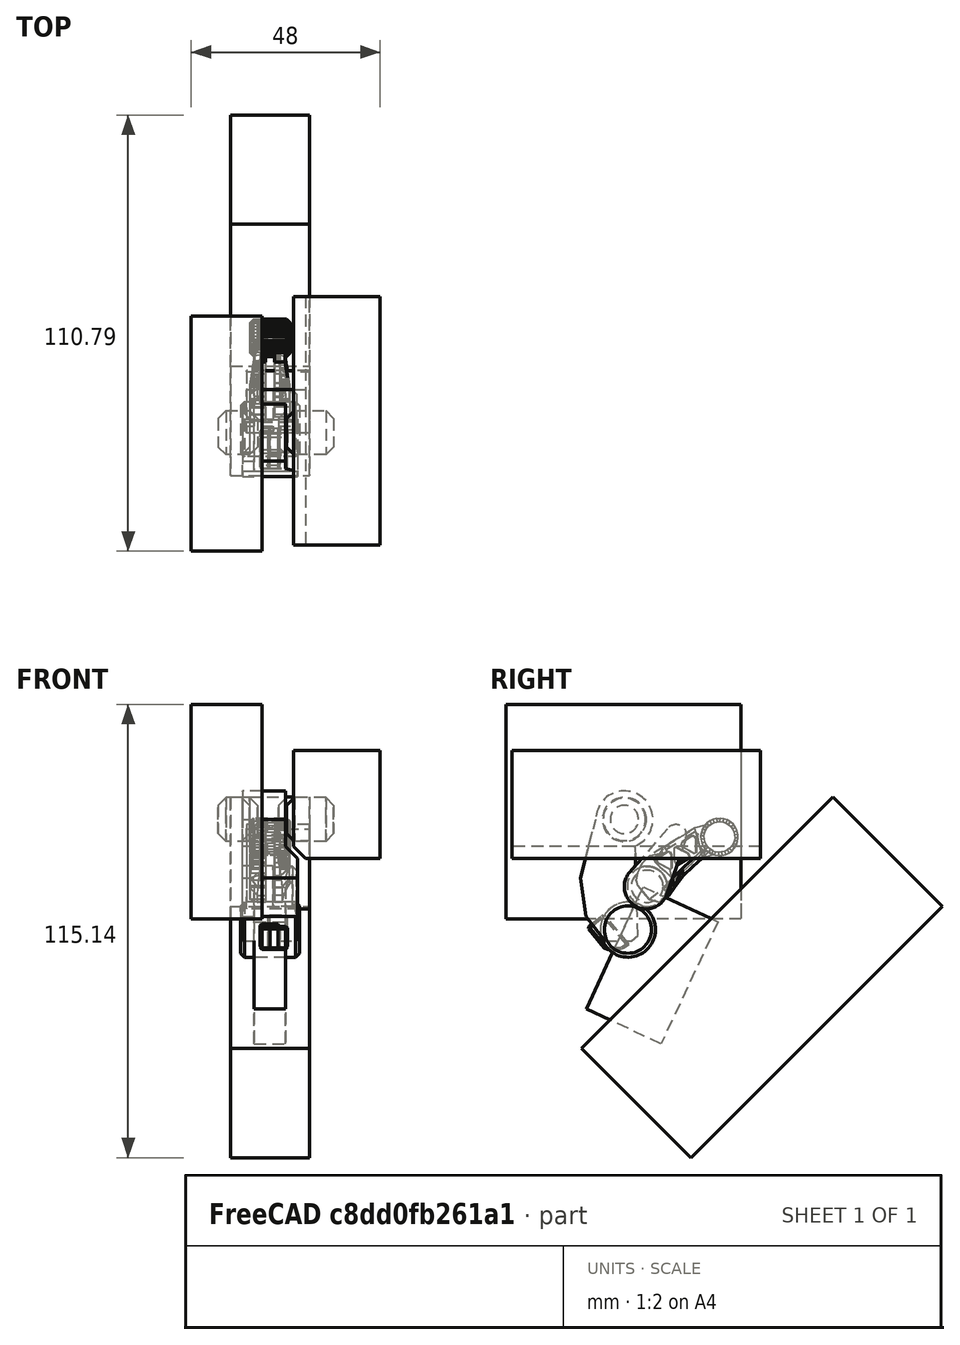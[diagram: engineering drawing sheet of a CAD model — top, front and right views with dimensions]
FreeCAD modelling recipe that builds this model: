
FCSTD DOCUMENT  (FreeCAD 0.21R33771 (Git))
Label: MechaLeg01
License: All rights reserved
LicenseURL: http://en.wikipedia.org/wiki/All_rights_reserved
objects: PartDesign::Body×12, Sketcher::SketchObject×11, PartDesign::Pad×11, PartDesign::Boolean×7, PartDesign::Chamfer×6, Part::Feature×2, Mesh::Feature×1, Part::Refine×1, PartDesign::FeatureBase×1
note: 68 computed .brp shape members not serialized (recipe doc carries the construction recipe); baked Part::Feature solids carry a one-line shape summary decoded from their .brp

FEATURE [Sketcher::SketchObject] Sketch
  FullyConstrained = false
  MapMode = 5
  Placement = pos=(0,0,0) rot=(0.57735,0.57735,0.57735;2.0944rad)
  Support = -> [YZ_Plane]
  sketch-geometry (7):
    g0: LineSegment StartX=-4.95735 StartY=-30.9168 StartZ=0 EndX=-9.7066 EndY=-24.689 EndZ=0
    g1: ArcOfCircle CenterX=0 CenterY=0 CenterZ=0 NormalX=0 NormalY=0 NormalZ=1 AngleXU=0 Radius=7.23735 StartAngle=5.09534 EndAngle=9.42478
    g2: LineSegment StartX=-4.95735 StartY=-30.9168 StartZ=0 EndX=1.76245 EndY=-30.9168 EndZ=0
    g3: LineSegment StartX=1.76245 StartY=-30.9168 StartZ=0 EndX=3.46482 EndY=-29.4243 EndZ=0
    g4: LineSegment StartX=3.46482 StartY=-29.4243 StartZ=0 EndX=2.70427 EndY=-6.71313 EndZ=0
    g5: LineSegment StartX=-9.7066 StartY=-24.689 StartZ=0 EndX=-11.1541 EndY=-14.812 EndZ=0
    g6: LineSegment StartX=-11.1541 StartY=-14.812 StartZ=0 EndX=-7.23735 EndY=1.8e-15 EndZ=0
  constraints (10):
    c: PointOnObject(g1,g-1)
    c: Coincident(g1,g-1)
    c: Coincident(g2,g0)
    c: Horizontal(g2)
    c: Coincident(g3,g2)
    c: Coincident(g4,g3)
    c: Coincident(g1,g4)
    c: Coincident(g5,g0)
    c: Coincident(g6,g5)
    c: Coincident(g6,g1)
FEATURE [PartDesign::Pad] Pad
  Direction = (1,-2e-16,3e-16)
  Length = 14
  Length2 = 10
  Placement = pos=(0,0,0) rot=(1,1,1;2.0944rad)
  Profile = -> Sketch
  ReferenceAxis = -> Sketch [N_Axis]
  Type = 0
FEATURE [Sketcher::SketchObject] Sketch001
  FullyConstrained = false
  MapMode = 5
  Placement = pos=(0,0,0) rot=(0.57735,0.57735,0.57735;2.0944rad)
  Support = -> [YZ_Plane001]
  sketch-geometry (1):
    g0: Circle CenterX=0 CenterY=0 CenterZ=0 NormalX=0 NormalY=0 NormalZ=1 AngleXU=0 Radius=5.59018
  constraints (1):
    c: Coincident(g0,g-1)
FEATURE [PartDesign::Pad] Pad001
  Direction = (1,-2e-16,3e-16)
  Length = 10
  Length2 = 10
  Placement = pos=(0,0,0) rot=(0.57735,0.57735,0.57735;2.0944rad)
  Profile = -> Sketch001
  ReferenceAxis = -> Sketch001 [N_Axis]
  Type = 0
FEATURE [PartDesign::Chamfer] Chamfer001
  Angle = 45
  Base = -> Pad001 [Face3,Face2]
  BaseFeature = -> Pad001
  ChamferType = 0
  FlipDirection = false
  Placement = pos=(0,0,0) rot=(0.57735,0.57735,0.57735;2.0944rad)
  Size = 2
  Size2 = 1
  SupportTransform = false
  UseAllEdges = false
FEATURE [PartDesign::Body] Body001  label="BodyCircleCutter01"
  Group = -> [Sketch001,Pad001,Chamfer001]
  Origin = -> Origin001
  Placement = pos=(-8.2,0,0) rot=(7,0,1;0rad)
  Tip = -> Chamfer001
FEATURE [Sketcher::SketchObject] Sketch002
  FullyConstrained = false
  MapMode = 5
  Placement = pos=(0,0,0) rot=(0.57735,0.57735,0.57735;2.0944rad)
  Support = -> [YZ_Plane002]
  sketch-geometry (1):
    g0: Circle CenterX=0 CenterY=0 CenterZ=0 NormalX=0 NormalY=0 NormalZ=1 AngleXU=0 Radius=5.59018
  constraints (1):
    c: Coincident(g0,g-1)
FEATURE [PartDesign::Pad] Pad002
  Direction = (1,-2e-16,3e-16)
  Length = 12
  Length2 = 10
  Placement = pos=(0,0,0) rot=(0.57735,0.57735,0.57735;2.0944rad)
  Profile = -> Sketch002
  ReferenceAxis = -> Sketch002 [N_Axis]
  Type = 0
FEATURE [PartDesign::Chamfer] Chamfer002
  Angle = 45
  Base = -> Pad002 [Face3,Face2]
  BaseFeature = -> Pad002
  ChamferType = 0
  FlipDirection = false
  Placement = pos=(0,0,0) rot=(0.57735,0.57735,0.57735;2.0944rad)
  Size = 2
  Size2 = 1
  SupportTransform = false
  UseAllEdges = false
FEATURE [PartDesign::Body] Body002  label="BodyCircleCutter02"
  Group = -> [Sketch002,Pad002,Chamfer002]
  Origin = -> Origin002
  Placement = pos=(9.2,0,0) rot=(0,0,1;0rad)
  Tip = -> Chamfer002
FEATURE [PartDesign::Boolean] Boolean  label="BodyCircleCutter1"
  BaseFeature = -> Pad
  Group = -> [Body001]
  Type = 1
FEATURE [PartDesign::Boolean] Boolean001  label="BodyCircleCutter2"
  BaseFeature = -> Boolean
  Group = -> [Body002]
  Type = 1
FEATURE [Sketcher::SketchObject] Sketch003
  FullyConstrained = false
  MapMode = 5
  Placement = pos=(0,0,0) rot=(0.57735,0.57735,0.57735;2.0944rad)
  Support = -> [YZ_Plane003]
  sketch-geometry (1):
    g0: Circle CenterX=0 CenterY=0 CenterZ=0 NormalX=0 NormalY=0 NormalZ=1 AngleXU=0 Radius=5.07389
  constraints (1):
    c: Coincident(g0,g-1)
FEATURE [PartDesign::Pad] Pad003
  Direction = (1,-2e-16,3e-16)
  Length = 9
  Length2 = 10
  Placement = pos=(0,0,0) rot=(0.57735,0.57735,0.57735;2.0944rad)
  Profile = -> Sketch003
  ReferenceAxis = -> Sketch003 [N_Axis]
  Type = 0
FEATURE [PartDesign::Chamfer] Chamfer003
  Angle = 45
  Base = -> Pad003 [Face3,Face2]
  BaseFeature = -> Pad003
  ChamferType = 0
  FlipDirection = false
  Placement = pos=(0,0,0) rot=(0.57735,0.57735,0.57735;2.0944rad)
  Size = 1
  Size2 = 1
  SupportTransform = false
  UseAllEdges = false
FEATURE [Sketcher::SketchObject] Sketch004
  FullyConstrained = false
  MapMode = 5
  Placement = pos=(0,0,0) rot=(0.57735,0.57735,0.57735;2.0944rad)
  Support = -> [YZ_Plane004]
  sketch-geometry (5):
    g0: LineSegment StartX=-9.41206 StartY=-26.5743 StartZ=0 EndX=-4.80637 EndY=-32.0632 EndZ=0
    g1: LineSegment StartX=-4.80637 StartY=-32.0632 StartZ=0 EndX=-0.621748 EndY=-32.0632 EndZ=0
    g2: LineSegment StartX=-0.621748 StartY=-32.0632 StartZ=0 EndX=1.19031 EndY=-30.7944 EndZ=0
    g3: LineSegment StartX=1.19031 StartY=-30.7944 StartZ=0 EndX=-5.2683 EndY=-23.0973 EndZ=0
    g4: LineSegment StartX=-9.41206 StartY=-26.5743 StartZ=0 EndX=-5.2683 EndY=-23.0973 EndZ=0
  constraints (6):
    c: Coincident(g1,g0)
    c: Horizontal(g1)
    c: Coincident(g2,g1)
    c: Coincident(g3,g2)
    c: Coincident(g4,g0)
    c: Coincident(g4,g3)
FEATURE [PartDesign::Pad] Pad004
  Direction = (1,-2e-16,3e-16)
  Length = 5
  Length2 = 10
  Placement = pos=(0,0,0) rot=(0.57735,0.57735,0.57735;2.0944rad)
  Profile = -> Sketch004
  ReferenceAxis = -> Sketch004 [N_Axis]
  Type = 0
FEATURE [PartDesign::Chamfer] Chamfer004
  Angle = 45
  Base = -> Pad004 [Face5,Face6,Face7,Face2]
  BaseFeature = -> Pad004
  ChamferType = 0
  FlipDirection = false
  Placement = pos=(0,0,0) rot=(0.57735,0.57735,0.57735;2.0944rad)
  Size = 0.5
  Size2 = 1
  SupportTransform = false
  UseAllEdges = false
FEATURE [PartDesign::Body] Body004  label="BodyKneeChunk"
  Group = -> [Sketch004,Pad004,Chamfer004]
  Origin = -> Origin004
  Placement = pos=(4.5,0,-0.9) rot=(0,0,1;0rad)
  Tip = -> Chamfer004
FEATURE [PartDesign::Boolean] Boolean002  label="BodyKneeChunk001"
  BaseFeature = -> Boolean001
  Group = -> [Body004]
  Type = 0
FEATURE [Sketcher::SketchObject] Sketch006
  FullyConstrained = false
  MapMode = 5
  Placement = pos=(0,0,0) rot=(0.57735,0.57735,0.57735;2.0944rad)
  Support = -> [YZ_Plane006]
  sketch-geometry (4):
    g0: ArcOfCircle CenterX=0 CenterY=0 CenterZ=0 NormalX=0 NormalY=0 NormalZ=1 AngleXU=0 Radius=5.59289 StartAngle=2.94959 EndAngle=6.47744
    g1: ArcOfCircle CenterX=0 CenterY=15.1041 CenterZ=0 NormalX=0 NormalY=0 NormalZ=1 AngleXU=0 Radius=2.71561 StartAngle=0.026149 EndAngle=3.00996
    g2: LineSegment StartX=-2.69212 StartY=15.4605 StartZ=0 EndX=-5.49012 EndY=1.06726 EndZ=0
    g3: LineSegment StartX=2.71468 StartY=15.1751 StartZ=0 EndX=5.4877 EndY=1.0796 EndZ=0
  constraints (6):
    c: Coincident(g0,g-1)
    c: PointOnObject(g1,g-2)
    c: Coincident(g1,g2)
    c: Coincident(g1,g3)
    c: Tangent(g0,g3) = 1.5708
    c: Tangent(g0,g2) = -1.5708
FEATURE [PartDesign::Pad] Pad006
  Direction = (1,-2e-16,3e-16)
  Length = 16
  Length2 = 10
  Placement = pos=(0,0,0) rot=(0.57735,0.57735,0.57735;2.0944rad)
  Profile = -> Sketch006
  ReferenceAxis = -> Sketch006 [N_Axis]
  Type = 0
FEATURE [PartDesign::Body] Body006  label="BodyKneeLowerCylinderCutter"
  Group = -> [Sketch006,Pad006]
  Origin = -> Origin006
  Placement = pos=(-1,5.56724,-17.1055) rot=(-1,0,0;0.523599rad)
  Tip = -> Pad006
FEATURE [PartDesign::Boolean] Boolean003  label="BodyKneeLowerCylinderCutter001"
  BaseFeature = -> Boolean002
  Group = -> [Body006]
  Type = 1
FEATURE [Sketcher::SketchObject] Sketch007
  FullyConstrained = false
  MapMode = 5
  Placement = pos=(0,0,0) rot=(0.57735,0.57735,0.57735;2.0944rad)
  Support = -> [YZ_Plane007]
  sketch-geometry (4):
    g0: LineSegment StartX=-21.0834 StartY=29.3575 StartZ=0 EndX=18.2412 EndY=29.3575 EndZ=0
    g1: LineSegment StartX=18.2412 StartY=29.3575 StartZ=0 EndX=18.2412 EndY=-60.8806 EndZ=0
    g2: LineSegment StartX=18.2412 StartY=-60.8806 StartZ=0 EndX=-21.0834 EndY=-60.8806 EndZ=0
    g3: LineSegment StartX=-21.0834 StartY=-60.8806 StartZ=0 EndX=-21.0834 EndY=29.3575 EndZ=0
  constraints (8):
    c: Coincident(g0,g1)
    c: Coincident(g1,g2)
    c: Coincident(g2,g3)
    c: Coincident(g3,g0)
    c: Horizontal(g0)
    c: Horizontal(g2)
    c: Vertical(g1)
    c: Vertical(g3)
FEATURE [PartDesign::Pad] Pad007
  Direction = (1,-2e-16,3e-16)
  Length = 20
  Length2 = 10
  Placement = pos=(0,0,0) rot=(0.57735,0.57735,0.57735;2.0944rad)
  Profile = -> Sketch007
  ReferenceAxis = -> Sketch007 [N_Axis]
  Type = 0
FEATURE [PartDesign::Body] Body007  label="BodyBase"
  Group = -> [Sketch007,Pad007]
  Origin = -> Origin007
  Placement = pos=(-5,47.0933,-29.9813) rot=(-1,0,0;0.785398rad)
  Tip = -> Pad007
FEATURE [Mesh::Feature] DudeBaseOperatorLegFoot
  Placement = pos=(5,24.1439,-4.44237) rot=(1,0,0;3.83972rad)
FEATURE [Part::Feature] DudeBaseOperatorLegFoot001_solid  label="DudeBaseOperatorLegFoot001 (Solid)"
  shape: bbox 10.16 x 25.95 x 21.36 mm, 1360 faces (baked)
FEATURE [Part::Feature] DudeBaseOperatorLegFoot001
  shape: bbox 10.16 x 25.95 x 21.36 mm, 1360 faces, 0 solids (baked)
FEATURE [Part::Refine] DudeBaseOperatorLegFoot001_solid001  label="DudeBaseOperatorLegFoot001 (Solid)001"
  Source = -> DudeBaseOperatorLegFoot001_solid
FEATURE [Sketcher::SketchObject] Sketch008
  FullyConstrained = false
  MapMode = 5
  Placement = pos=(0,0,0) rot=(0.57735,0.57735,0.57735;2.0944rad)
  Support = -> [YZ_Plane010]
  sketch-geometry (4):
    g0: LineSegment StartX=-30.0375 StartY=29.2055 StartZ=0 EndX=29.6527 EndY=29.2055 EndZ=0
    g1: LineSegment StartX=29.6527 StartY=29.2055 StartZ=0 EndX=29.6527 EndY=-25.2796 EndZ=0
    g2: LineSegment StartX=29.6527 StartY=-25.2796 StartZ=0 EndX=-30.0375 EndY=-25.2796 EndZ=0
    g3: LineSegment StartX=-30.0375 StartY=-25.2796 StartZ=0 EndX=-30.0375 EndY=29.2055 EndZ=0
  constraints (8):
    c: Coincident(g0,g1)
    c: Coincident(g1,g2)
    c: Coincident(g2,g3)
    c: Coincident(g3,g0)
    c: Horizontal(g0)
    c: Horizontal(g2)
    c: Vertical(g1)
    c: Vertical(g3)
FEATURE [PartDesign::Pad] Pad008
  Direction = (1,-2e-16,3e-16)
  Length = 18
  Length2 = 10
  Placement = pos=(0,0,0) rot=(0.57735,0.57735,0.57735;2.0944rad)
  Profile = -> Sketch008
  ReferenceAxis = -> Sketch008 [N_Axis]
  Type = 0
FEATURE [PartDesign::Body] Body010  label="BodyCutter"
  Group = -> [Sketch008,Pad008]
  Origin = -> Origin010
  Placement = pos=(-15,0,0) rot=(0,0,1;0rad)
  Tip = -> Pad008
FEATURE [PartDesign::Boolean] Boolean004
  BaseFeature = -> Chamfer003
  Group = -> [Body010]
  Type = 1
FEATURE [PartDesign::Body] Body003  label="BodyKneeLowerCylinder"
  Group = -> [Sketch003,Pad003,Chamfer003,Boolean004]
  Origin = -> Origin003
  Placement = pos=(2.8,5.8,-17) rot=(0,0,1;0rad)
  Tip = -> Boolean004
FEATURE [Sketcher::SketchObject] Sketch009
  FullyConstrained = true
  MapMode = 5
  Placement = pos=(0,0,0) rot=(0.57735,0.57735,0.57735;2.0944rad)
  Support = -> [YZ_Plane011]
  sketch-geometry (1):
    g0: Circle CenterX=0 CenterY=0 CenterZ=0 NormalX=0 NormalY=0 NormalZ=1 AngleXU=0 Radius=7
  constraints (2):
    c: Coincident(g0,g-1)
    c: Diameter(g0) = 14
FEATURE [PartDesign::Pad] Pad009
  Direction = (1,-2e-16,3e-16)
  Length = 15
  Length2 = 10
  Placement = pos=(0,0,0) rot=(0.57735,0.57735,0.57735;2.0944rad)
  Profile = -> Sketch009
  ReferenceAxis = -> Sketch009 [N_Axis]
  Type = 0
FEATURE [PartDesign::Chamfer] Chamfer007
  Angle = 45
  Base = -> Pad009 [Face3,Face2]
  BaseFeature = -> Pad009
  ChamferType = 0
  FlipDirection = false
  Placement = pos=(0,0,0) rot=(0.57735,0.57735,0.57735;2.0944rad)
  Size = 1
  Size2 = 1
  SupportTransform = false
  UseAllEdges = false
FEATURE [PartDesign::Body] Body011  label="BodyKneeCover"
  Group = -> [Sketch009,Pad009,Chamfer007]
  Origin = -> Origin011
  Placement = pos=(-2.5,0.9,-28) rot=(0,0,1;0rad)
  Tip = -> Chamfer007
FEATURE [Sketcher::SketchObject] Sketch010
  FullyConstrained = false
  MapMode = 5
  Placement = pos=(0,0,0) rot=(0.57735,0.57735,0.57735;2.0944rad)
  Support = -> [YZ_Plane012]
  sketch-geometry (4):
    g0: LineSegment StartX=0 StartY=12.2334 StartZ=0 EndX=20.98 EndY=12.2334 EndZ=0
    g1: LineSegment StartX=20.98 StartY=12.2334 StartZ=0 EndX=20.98 EndY=-21.9944 EndZ=0
    g2: LineSegment StartX=20.98 StartY=-21.9944 StartZ=0 EndX=0 EndY=-21.9944 EndZ=0
    g3: LineSegment StartX=0 StartY=-21.9944 StartZ=0 EndX=0 EndY=12.2334 EndZ=0
  constraints (9):
    c: Coincident(g0,g1)
    c: Coincident(g1,g2)
    c: Coincident(g2,g3)
    c: Coincident(g3,g0)
    c: Horizontal(g0)
    c: Horizontal(g2)
    c: Vertical(g1)
    c: Vertical(g3)
    c: PointOnObject(g0,g-2)
FEATURE [PartDesign::Pad] Pad010
  Direction = (1,-2e-16,3e-16)
  Length = 8
  Length2 = 10
  Placement = pos=(0,0,0) rot=(0.57735,0.57735,0.57735;2.0944rad)
  Profile = -> Sketch010
  ReferenceAxis = -> Sketch010 [N_Axis]
  Type = 0
FEATURE [PartDesign::Body] Body012  label="BodyKneeCapCutter"
  Group = -> [Sketch010,Pad010]
  Origin = -> Origin012
  Placement = pos=(1,-0.381386,-28.2357) rot=(-1,0,0;0.436332rad)
  Tip = -> Pad010
FEATURE [PartDesign::FeatureBase] BaseFeature
  BaseFeature = -> DudeBaseOperatorLegFoot001_solid001
FEATURE [PartDesign::Boolean] Boolean007
  BaseFeature = -> BaseFeature
  Group = -> [Body003]
  Type = 0
FEATURE [PartDesign::Body] Body008  label="BodyLowerLegStandIn"
  BaseFeature = -> DudeBaseOperatorLegFoot001_solid001
  Group = -> [BaseFeature,Boolean007]
  Origin = -> Origin008
  Tip = -> Boolean007
FEATURE [Sketcher::SketchObject] Sketch011
  FullyConstrained = false
  MapMode = 5
  Placement = pos=(0,0,0) rot=(0.57735,0.57735,0.57735;2.0944rad)
  Support = -> [YZ_Plane013]
  sketch-geometry (4):
    g0: LineSegment StartX=-28.5152 StartY=17.4751 StartZ=0 EndX=34.6119 EndY=17.4751 EndZ=0
    g1: LineSegment StartX=34.6119 StartY=17.4751 StartZ=0 EndX=34.6119 EndY=-9.87656 EndZ=0
    g2: LineSegment StartX=34.6119 StartY=-9.87656 StartZ=0 EndX=-28.5152 EndY=-9.87656 EndZ=0
    g3: LineSegment StartX=-28.5152 StartY=-9.87656 StartZ=0 EndX=-28.5152 EndY=17.4751 EndZ=0
  constraints (8):
    c: Coincident(g0,g1)
    c: Coincident(g1,g2)
    c: Coincident(g2,g3)
    c: Coincident(g3,g0)
    c: Horizontal(g0)
    c: Horizontal(g2)
    c: Vertical(g1)
    c: Vertical(g3)
FEATURE [PartDesign::Pad] Pad011
  Direction = (1,-2e-16,3e-16)
  Length = 22
  Length2 = 10
  Placement = pos=(0,0,0) rot=(1,1,1;2.0944rad)
  Profile = -> Sketch011
  ReferenceAxis = -> Sketch011 [N_Axis]
  Type = 0
FEATURE [PartDesign::Chamfer] Chamfer
  Angle = 45
  Base = -> Pad011 [Edge9]
  BaseFeature = -> Pad011
  ChamferType = 0
  FlipDirection = false
  Placement = pos=(0,0,0) rot=(1,1,1;2.0944rad)
  Size = 3
  Size2 = 1
  SupportTransform = false
  UseAllEdges = false
FEATURE [PartDesign::Body] Body013  label="AngleCutter"
  Group = -> [Sketch011,Pad011,Chamfer]
  Origin = -> Origin013
  Placement = pos=(11,0,0) rot=(0,0,1;0rad)
  Tip = -> Chamfer
FEATURE [PartDesign::Boolean] Boolean008
  BaseFeature = -> Boolean003
  Group = -> [Body013]
  Type = 1
FEATURE [PartDesign::Body] Body  label="BodyUpperLeg"
  Group = -> [Sketch,Pad,Boolean,Boolean001,Boolean002,Boolean003,Boolean008]
  Origin = -> Origin
  Placement = pos=(-2,0,0) rot=(0,0,1;0rad)
  Tip = -> Boolean008
